# Revit family: CoilingDoor_Metal_WayneDalton_IntegralFrame
name_source: partatom
category: Doors
units: mm (PartAtom-declared; Revit-internal decimal feet)

## family parameters
Always vertical = Yes
Cut with Voids When Loaded = No
Host = Wall
Room Calculation Point = No
Shared = No

## types (1)
- CoilingDoor_Metal_WayneDalton_IntegralFrame
    Assembly Code = B2030400
    Base Rail Depth = 0' - 0 1/2"
    Base Rail Height = 0' - 2"
    Bracket Height = 4' - 0"
    Curtain Material = Metal - Alum Slats - Wayne Dalton - Anodized - Bronze
    Description = Wayne-Dalton Coiling Counter Door as Specified
    Door Frame Material = Metal - Aluminum - Wayne Dalton - Anodized - Bronze
    Expected Lifespan (Years) = 0
    Fire Rating = As Specified
    Frame Thickness = 0' - 3"
    Function = Interior
    Height = 4' - 0"
    Hood Depth = 0' - 9 1/8"
    Hood Height = 0' - 9 1/2"
    Jamb Thickness_Sides = 0' - 3"
    Keynote = 08332
    Maintenance Schedule (Months) = 0
    Manufacturer = Wayne-Dalton Corp.
    Manufacturer Website = http://commercial.wayne-dalton.com
    Model = As Specified in 08332
    Product Data = http://arcat.com
    R-Value = 0
    RO Spacing Sides = 0' - 0"
    RO Spacing Top = 0' - 0"
    Rough Height = 4' - 0"
    Rough Width = 5' - 0"
    Sales Information = http://commercial.wayne-dalton.com
    Send Message = http://www.arcat.com
    Sill Thickness = 0' - 1 1/2"
    Specification = http://arcat.com
    URL = http://commercial.wayne-dalton.com
    Wall Closure = By host
    Warranty Duration (Years) = 0
    Width = 5' - 0"

## geometry (parser evidence)
native form markers: Blend x67, Sweep x11
no freeform markers — native parametric forms only
